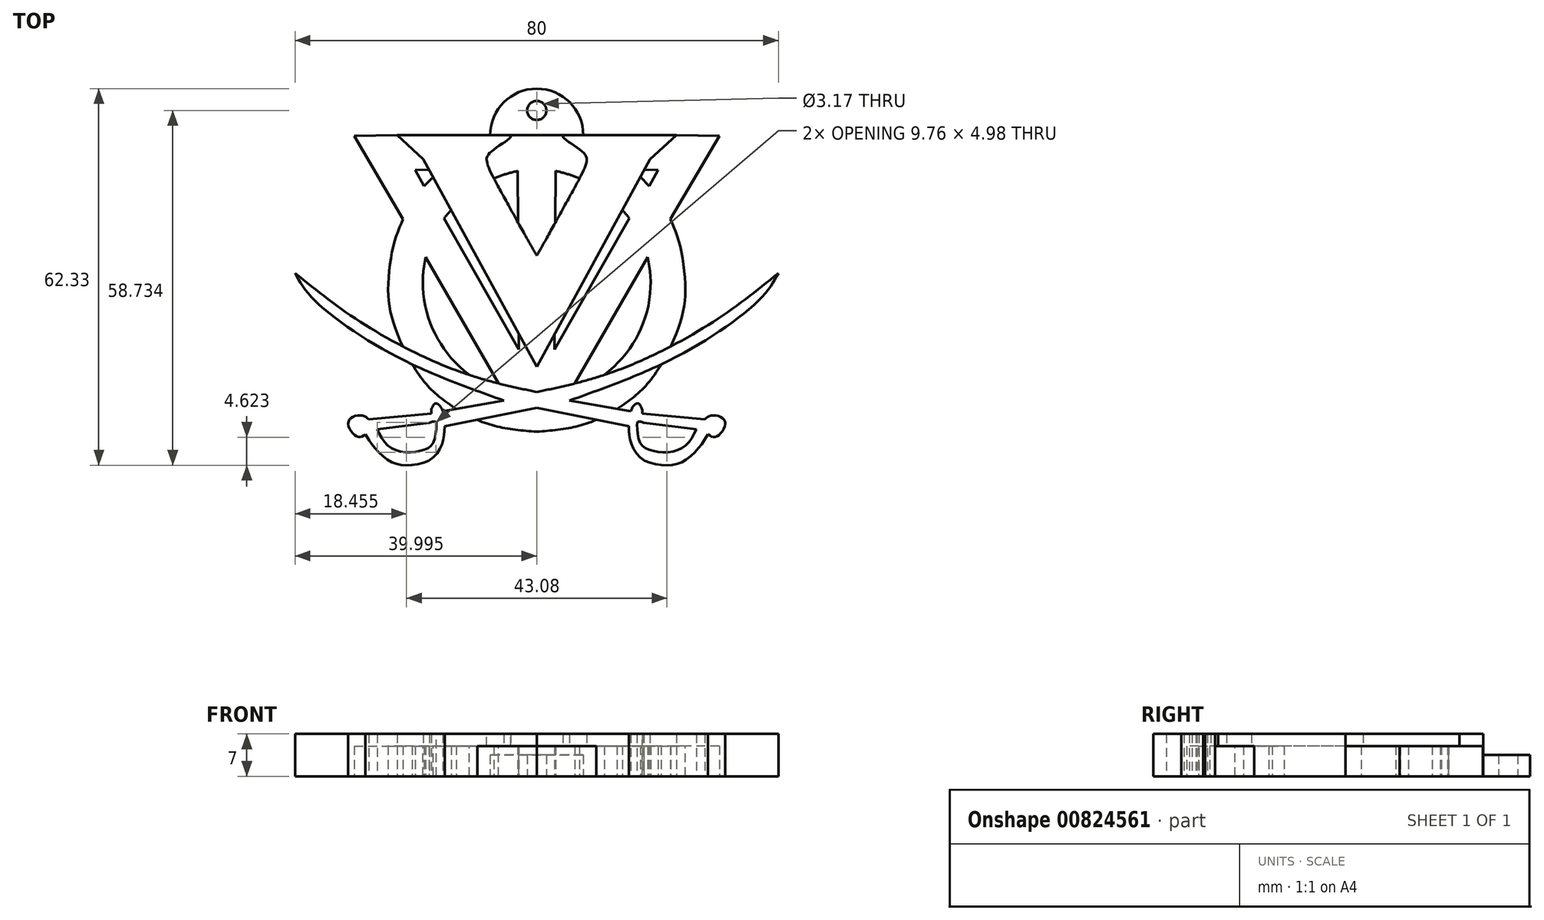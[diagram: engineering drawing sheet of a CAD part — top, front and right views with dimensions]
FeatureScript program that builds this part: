
annotation { "Feature Type Name" : "Feature", "Feature Type Description" : "" }
export const myFeature = defineFeature(function(context is Context, id is Id, definition is map)
    precondition{}
    {
        {
            var Q0;
            Q0=qCreatedBy(makeId("Top.planeOp"),FACE);
            var sketch = newSketch(context, id + "F0", { "sketchPlane" : qUnion([Q0])});
            skLineSegment(sketch, "E0", {"start": v(-25.22, 10.5) * mm, "end": v(-6.43, 10.5) * mm});
            skLineSegment(sketch, "E1", {"start": v(-25.22, 10.5) * mm, "end": v(-20.86, 6.51) * mm});
            skLineSegment(sketch, "E2", {"start": v(-20.86, 6.51) * mm, "end": v(-2.11, -27.86) * mm});
            skFitSpline(sketch, "E3", {"points": [v(-2.11, -32.02) * mm, v(-15.16, -28.54) * mm, v(-31.06, -20.55) * mm, v(-42.11, -12.34) * mm], "startDerivative": vector(-39.94, 8.48) * mm, "endDerivative": vector(-32.07, 25.88) * mm});
            skFitSpline(sketch, "E4", {"points": [v(-42.11, -12.34) * mm, v(-39.28, -16.4) * mm, v(-26.1, -25.73) * mm, v(-7.53, -33.43) * mm], "startDerivative": vector(9.94, -18.28) * mm, "endDerivative": vector(45.1, -16.07) * mm});
            skFitSpline(sketch, "E5", {"points": [v(-7.53, -33.43) * mm, v(-17.67, -35.2) * mm], "startDerivative": vector(-10.14, -1.78) * mm, "endDerivative": vector(-10.14, -1.78) * mm});
            skFitSpline(sketch, "E6", {"points": [v(-17.67, -35.2) * mm, v(-18.15, -34.28) * mm, v(-18.87, -33.9) * mm, v(-19.52, -34.81) * mm, v(-19.58, -35.55) * mm], "startDerivative": vector(-1.44, 3.67) * mm, "endDerivative": vector(0.2, -2.99) * mm});
            skFitSpline(sketch, "E7", {"points": [v(-19.58, -35.55) * mm, v(-29.94, -36.56) * mm], "startDerivative": vector(-10.36, -1.01) * mm, "endDerivative": vector(-10.36, -1.01) * mm});
            skFitSpline(sketch, "E8", {"points": [v(-29.94, -36.56) * mm, v(-30.68, -36) * mm, v(-32.31, -36.04) * mm, v(-33.32, -37.05) * mm, v(-32.66, -38.72) * mm, v(-31.48, -39.47) * mm, v(-30.46, -39.03) * mm], "startDerivative": vector(-4.52, 4.85) * mm, "endDerivative": vector(6.61, 4.5) * mm});
            skFitSpline(sketch, "E9", {"points": [v(-30.46, -39.03) * mm, v(-29.4, -40.66) * mm, v(-26.68, -43.34) * mm, v(-23.6, -44.13) * mm, v(-19.58, -43.12) * mm, v(-17.67, -40.26) * mm, v(-17.35, -37.7) * mm], "startDerivative": vector(6.67, -11.42) * mm, "endDerivative": vector(0.59, 16.46) * mm});
            skLineSegment(sketch, "E10", {"start": v(-17.35, -37.7) * mm, "end": v(-2.11, -34.63) * mm});
            skFitSpline(sketch, "E11", {"points": [v(-6.43, 10.5) * mm, v(-6.52, 10.1) * mm, v(-8.55, 8.64) * mm, v(-10.26, 7.08) * mm, v(-10.38, 6.19) * mm, v(-9.8, 4.56) * mm, v(-7.67, 0.53) * mm, v(-3.54, -6.95) * mm, v(-2.11, -9.4) * mm], "startDerivative": vector(0.4, -7.36) * mm, "endDerivative": vector(9.07, -15.38) * mm});
            skFitSpline(sketch, "E12.MirrorCS", {"points": [v(2.2, 10.5) * mm, v(2.29, 10.1) * mm, v(4.32, 8.64) * mm, v(6.03, 7.08) * mm, v(6.15, 6.19) * mm, v(5.58, 4.56) * mm, v(3.44, 0.53) * mm, v(-0.7, -6.95) * mm, v(-2.11, -9.4) * mm], "startDerivative": vector(-0.4, -7.36) * mm, "endDerivative": vector(-9.07, -15.38) * mm});
            skLineSegment(sketch, "E13.MirrorCS", {"start": v(20.99, 10.5) * mm, "end": v(2.2, 10.5) * mm});
            skLineSegment(sketch, "E14.MirrorCS", {"start": v(16.63, 6.51) * mm, "end": v(-2.11, -27.86) * mm});
            skLineSegment(sketch, "E15.MirrorCS", {"start": v(20.99, 10.5) * mm, "end": v(16.63, 6.51) * mm});
            skFitSpline(sketch, "E16.MirrorCS", {"points": [v(-2.11, -32.02) * mm, v(10.93, -28.54) * mm, v(26.83, -20.55) * mm, v(37.89, -12.34) * mm], "startDerivative": vector(39.94, 8.48) * mm, "endDerivative": vector(32.07, 25.88) * mm});
            skFitSpline(sketch, "E17.MirrorCS", {"points": [v(37.89, -12.34) * mm, v(35.05, -16.4) * mm, v(21.88, -25.73) * mm, v(3.3, -33.43) * mm], "startDerivative": vector(-9.94, -18.28) * mm, "endDerivative": vector(-45.1, -16.07) * mm});
            skFitSpline(sketch, "E18.MirrorCS", {"points": [v(3.3, -33.43) * mm, v(13.44, -35.2) * mm], "startDerivative": vector(10.14, -1.78) * mm, "endDerivative": vector(10.14, -1.78) * mm});
            skFitSpline(sketch, "E19.MirrorCS", {"points": [v(13.44, -35.2) * mm, v(13.92, -34.28) * mm, v(14.64, -33.9) * mm, v(15.3, -34.81) * mm, v(15.35, -35.55) * mm], "startDerivative": vector(1.44, 3.67) * mm, "endDerivative": vector(-0.2, -2.99) * mm});
            skFitSpline(sketch, "E20.MirrorCS", {"points": [v(15.35, -35.55) * mm, v(25.7, -36.56) * mm], "startDerivative": vector(10.36, -1.01) * mm, "endDerivative": vector(10.36, -1.01) * mm});
            skFitSpline(sketch, "E21.MirrorCS", {"points": [v(25.7, -36.56) * mm, v(26.46, -36) * mm, v(28.08, -36.04) * mm, v(29.1, -37.05) * mm, v(28.43, -38.72) * mm, v(27.25, -39.47) * mm, v(26.24, -39.03) * mm], "startDerivative": vector(4.52, 4.85) * mm, "endDerivative": vector(-6.61, 4.5) * mm});
            skFitSpline(sketch, "E22.MirrorCS", {"points": [v(26.24, -39.03) * mm, v(25.18, -40.66) * mm, v(22.45, -43.34) * mm, v(19.37, -44.13) * mm, v(15.35, -43.12) * mm, v(13.44, -40.26) * mm, v(13.12, -37.7) * mm], "startDerivative": vector(-6.67, -11.42) * mm, "endDerivative": vector(-0.59, 16.46) * mm});
            skLineSegment(sketch, "E23.MirrorCS", {"start": v(13.12, -37.7) * mm, "end": v(-2.11, -34.63) * mm});
            skLineSegment(sketch, "E24", {"start": v(-32.33, 10.4) * mm, "end": v(-25.22, 10.5) * mm});
            skLineSegment(sketch, "E25", {"start": v(-6.43, 10.5) * mm, "end": v(-2.11, 10.5) * mm});
            skLineSegment(sketch, "E26", {"start": v(-32.33, 10.4) * mm, "end": v(-24.25, -3.37) * mm});
            skPoint(sketch, "E27.7.internal.snap0", {"position": v(-2.14, -38.58) * mm});
            skFitSpline(sketch, "E27", {"points": [v(-24.25, -3.37) * mm, v(-25.82, -7.77) * mm, v(-26.7, -15.3) * mm, v(-25.56, -21.37) * mm, v(-21.37, -29.48) * mm, v(-16.5, -34.08) * mm, v(-9.76, -37.43) * mm, v(-2.11, -38.58) * mm], "startDerivative": vector(-14.53, -34.1) * mm, "endDerivative": vector(51.7, -4.04) * mm});
            skLineSegment(sketch, "E28", {"start": v(-22.21, 4.74) * mm, "end": v(-20.74, 2.05) * mm});
            skLineSegment(sketch, "E29", {"start": v(-20.74, 2.05) * mm, "end": v(-18.02, 4.84) * mm});
            skLineSegment(sketch, "E30", {"start": v(-18.02, 4.84) * mm, "end": v(-22.21, 4.74) * mm});
            skLineSegment(sketch, "E31", {"start": v(-20.48, -9.7) * mm, "end": v(-7.56, -32.1) * mm});
            skFitSpline(sketch, "E32", {"points": [v(-20.48, -9.7) * mm, v(-20.95, -13.05) * mm, v(-20.48, -18.18) * mm, v(-18.65, -22.94) * mm, v(-15.83, -26.86) * mm, v(-11.48, -30.42) * mm, v(-7.56, -32.1) * mm], "startDerivative": vector(-4.35, -22.23) * mm, "endDerivative": vector(24.5, -8.47) * mm});
            skFitSpline(sketch, "E33", {"points": [v(-5.24, 4.58) * mm, v(-12.79, 1.4) * mm, v(-17.45, -3.26) * mm], "startDerivative": vector(-17.16, -3.73) * mm, "endDerivative": vector(-8.8, -10.76) * mm});
            skLineSegment(sketch, "E34", {"start": v(-17.45, -3.26) * mm, "end": v(-5.05, -25) * mm});
            skLineSegment(sketch, "E35", {"start": v(-5.05, -25) * mm, "end": v(-5.24, 4.58) * mm});
            skLineSegment(sketch, "E36.MirrorCS", {"start": v(0.82, -25) * mm, "end": v(1.01, 4.58) * mm});
            skFitSpline(sketch, "E37.MirrorCS", {"points": [v(1.01, 4.58) * mm, v(8.56, 1.4) * mm, v(13.22, -3.26) * mm], "startDerivative": vector(17.16, -3.73) * mm, "endDerivative": vector(8.8, -10.76) * mm});
            skLineSegment(sketch, "E38.MirrorCS", {"start": v(17.98, 4.74) * mm, "end": v(16.51, 2.05) * mm});
            skLineSegment(sketch, "E39.MirrorCS", {"start": v(16.51, 2.05) * mm, "end": v(13.8, 4.84) * mm});
            skLineSegment(sketch, "E40.MirrorCS", {"start": v(13.8, 4.84) * mm, "end": v(17.98, 4.74) * mm});
            skFitSpline(sketch, "E41.MirrorCS", {"points": [v(20.02, -3.37) * mm, v(21.6, -7.77) * mm, v(22.48, -15.3) * mm, v(21.33, -21.37) * mm, v(17.14, -29.48) * mm, v(12.28, -34.08) * mm, v(5.53, -37.43) * mm, v(-2.11, -38.58) * mm], "startDerivative": vector(14.53, -34.1) * mm, "endDerivative": vector(-51.7, -4.04) * mm});
            skFitSpline(sketch, "E42.MirrorCS", {"points": [v(16.25, -9.7) * mm, v(16.72, -13.05) * mm, v(16.25, -18.18) * mm, v(14.42, -22.94) * mm, v(11.6, -26.86) * mm, v(7.26, -30.42) * mm, v(3.33, -32.1) * mm], "startDerivative": vector(4.35, -22.23) * mm, "endDerivative": vector(-24.5, -8.47) * mm});
            skLineSegment(sketch, "E43.MirrorCS", {"start": v(16.25, -9.7) * mm, "end": v(3.33, -32.1) * mm});
            skLineSegment(sketch, "E44.MirrorCS", {"start": v(13.22, -3.26) * mm, "end": v(0.82, -25) * mm});
            skLineSegment(sketch, "E45.MirrorCS", {"start": v(28.1, 10.4) * mm, "end": v(20.02, -3.37) * mm});
            skLineSegment(sketch, "E46.MirrorCS", {"start": v(28.1, 10.4) * mm, "end": v(20.99, 10.5) * mm});
            skLineSegment(sketch, "E47.MirrorCS", {"start": v(2.2, 10.5) * mm, "end": v(-2.11, 10.5) * mm});
            skFitSpline(sketch, "E48", {"points": [v(-28.53, -38.17) * mm, v(-19.88, -37.1) * mm], "startDerivative": vector(8.66, 1.07) * mm, "endDerivative": vector(8.66, 1.07) * mm});
            skFitSpline(sketch, "E49", {"points": [v(-28.53, -38.17) * mm, v(-26.76, -40.87) * mm, v(-23.8, -41.98) * mm, v(-20.62, -41.53) * mm, v(-19.18, -40.27) * mm, v(-18.73, -37.46) * mm, v(-18.88, -36.9) * mm, v(-19.88, -37.1) * mm], "startDerivative": vector(8.42, -17.19) * mm, "endDerivative": vector(-12.37, -4.06) * mm});
            skFitSpline(sketch, "E50.MirrorCS", {"points": [v(24.3, -38.17) * mm, v(15.65, -37.1) * mm], "startDerivative": vector(-8.66, 1.07) * mm, "endDerivative": vector(-8.66, 1.07) * mm});
            skFitSpline(sketch, "E51.MirrorCS", {"points": [v(24.3, -38.17) * mm, v(22.53, -40.87) * mm, v(19.57, -41.98) * mm, v(16.39, -41.53) * mm, v(14.95, -40.27) * mm, v(14.5, -37.46) * mm, v(14.65, -36.9) * mm, v(15.65, -37.1) * mm], "startDerivative": vector(-8.42, -17.19) * mm, "endDerivative": vector(12.37, -4.06) * mm});
            skCircle(sketch, "E52", {"center": v(-2.11, 14.6) * mm, "radius": 1.59 * mm});
            skArc(sketch, "E53", {"start": v(5.6, 10.5) * mm, "mid": v(-2.11, 18.2) * mm, "end": v(-9.82, 10.5) * mm});
            skSolve(sketch);
        }
        {
            var Q0;
            {var subQ9=sQuery(id+"F0.wireOp",EDGE,"E0");Q0=makeQuery(id+"F0.imprint","IMPRINT",FACE,{"disambiguationData":[TD([[makeQuery(id+"F0.imprint","IMPRINT",EDGE,{"derivedFrom":subQ9}),-1.0]])]});}
            var Q1;
            {var subQ0=sQuery(id+"F0.wireOp",EDGE,"E33");var subQ1=sQuery(id+"F0.wireOp",EDGE,"E2");var subQ2=makeQuery(id+"F0.imprint","INTERSECT",VERTEX,{"derivedFrom":[subQ1,subQ0]});Q1=makeQuery(id+"F0.imprint","IMPRINT",FACE,{"disambiguationData":[TD([[makeQuery(id+"F0.imprint","IMPRINT",EDGE,{"disambiguationData":[TD([[subQ2,-1.0]])],"derivedFrom":subQ1}),1.0]])]});}
            var Q2;
            {var subQ0=sQuery(id+"F0.wireOp",EDGE,"E14.MirrorCS");var subQ1=sQuery(id+"F0.wireOp",EDGE,"E2");var subQ2=makeQuery(id+"F0.imprint","INTERSECT",VERTEX,{"derivedFrom":[subQ1,subQ0]});Q2=makeQuery(id+"F0.imprint","IMPRINT",FACE,{"disambiguationData":[TD([[makeQuery(id+"F0.imprint","IMPRINT",EDGE,{"disambiguationData":[TD([[subQ2,1.0]])],"derivedFrom":subQ1}),1.0]])]});}
            var Q3;
            {var subQ0=sQuery(id+"F0.wireOp",EDGE,"E37.MirrorCS");var subQ1=sQuery(id+"F0.wireOp",EDGE,"E12.MirrorCS");var subQ2=makeQuery(id+"F0.imprint","INTERSECT",VERTEX,{"derivedFrom":[subQ1,subQ0]});Q3=makeQuery(id+"F0.imprint","IMPRINT",FACE,{"disambiguationData":[TD([[makeQuery(id+"F0.imprint","IMPRINT",EDGE,{"disambiguationData":[TD([[subQ2,-1.0]])],"derivedFrom":subQ1}),1.0]])]});}
            var Q4;
            {var subQ8=sQuery(id+"F0.wireOp",EDGE,"E13.MirrorCS");Q4=makeQuery(id+"F0.imprint","IMPRINT",FACE,{"disambiguationData":[TD([[makeQuery(id+"F0.imprint","IMPRINT",EDGE,{"derivedFrom":subQ8}),1.0]])]});}
            var Q5;
            {var subQ0=sQuery(id+"F0.wireOp",EDGE,"E17.MirrorCS");var subQ1=sQuery(id+"F0.wireOp",EDGE,"E16.MirrorCS");var subQ2=makeQuery(id+"F0.imprint","INTERSECT",VERTEX,{"derivedFrom":[subQ1,subQ0]});Q5=makeQuery(id+"F0.imprint","IMPRINT",FACE,{"disambiguationData":[TD([[makeQuery(id+"F0.imprint","IMPRINT",EDGE,{"disambiguationData":[TD([[subQ2,1.0]])],"derivedFrom":subQ1}),-1.0]])]});}
            var Q6;
            {var subQ8=sQuery(id+"F0.wireOp",EDGE,"E3");var subQ14=sQuery(id+"F0.wireOp",EDGE,"E16.MirrorCS");var subQ24=makeQuery(id+"F0.imprint","INTERSECT",VERTEX,{"derivedFrom":[subQ8,subQ14]});Q6=makeQuery(id+"F0.imprint","IMPRINT",FACE,{"disambiguationData":[TD([[makeQuery(id+"F0.imprint","IMPRINT",EDGE,{"disambiguationData":[TD([[subQ24,-1.0]])],"derivedFrom":subQ8}),1.0]])]});}
            var Q7;
            {var subQ0=sQuery(id+"F0.wireOp",EDGE,"E31");var subQ1=sQuery(id+"F0.wireOp",EDGE,"E3");var subQ2=makeQuery(id+"F0.imprint","INTERSECT",VERTEX,{"derivedFrom":[subQ1,subQ0]});Q7=makeQuery(id+"F0.imprint","IMPRINT",FACE,{"disambiguationData":[TD([[makeQuery(id+"F0.imprint","IMPRINT",EDGE,{"disambiguationData":[TD([[subQ2,-1.0]])],"derivedFrom":subQ1}),1.0]])]});}
            var Q8;
            {var subQ0=sQuery(id+"F0.wireOp",EDGE,"E43.MirrorCS");var subQ1=sQuery(id+"F0.wireOp",EDGE,"E16.MirrorCS");var subQ2=makeQuery(id+"F0.imprint","INTERSECT",VERTEX,{"derivedFrom":[subQ1,subQ0]});Q8=makeQuery(id+"F0.imprint","IMPRINT",FACE,{"disambiguationData":[TD([[makeQuery(id+"F0.imprint","IMPRINT",EDGE,{"disambiguationData":[TD([[subQ2,-1.0]])],"derivedFrom":subQ1}),-1.0]])]});}
            var Q9;
            {var subQ0=sQuery(id+"F0.wireOp",EDGE,"E6");Q9=makeQuery(id+"F0.imprint","IMPRINT",FACE,{"disambiguationData":[TD([[makeQuery(id+"F0.imprint","IMPRINT",EDGE,{"derivedFrom":subQ0}),1.0]])]});}
            var Q10;
            {var subQ0=sQuery(id+"F0.wireOp",EDGE,"E19.MirrorCS");Q10=makeQuery(id+"F0.imprint","IMPRINT",FACE,{"disambiguationData":[TD([[makeQuery(id+"F0.imprint","IMPRINT",EDGE,{"derivedFrom":subQ0}),-1.0]])]});}
            var Q11;
            {var subQ0=sQuery(id+"F0.wireOp",EDGE,"E4");var subQ1=sQuery(id+"F0.wireOp",EDGE,"E3");var subQ2=makeQuery(id+"F0.imprint","INTERSECT",VERTEX,{"derivedFrom":[subQ1,subQ0]});Q11=makeQuery(id+"F0.imprint","IMPRINT",FACE,{"disambiguationData":[TD([[makeQuery(id+"F0.imprint","IMPRINT",EDGE,{"disambiguationData":[TD([[subQ2,1.0]])],"derivedFrom":subQ1}),1.0]])]});}
            var Q12;
            {var subQ0=sQuery(id+"F0.wireOp",EDGE,"E30");var subQ1=sQuery(id+"F0.wireOp",EDGE,"E2");var subQ2=makeQuery(id+"F0.imprint","INTERSECT",VERTEX,{"derivedFrom":[subQ1,subQ0]});Q12=makeQuery(id+"F0.imprint","IMPRINT",FACE,{"disambiguationData":[TD([[makeQuery(id+"F0.imprint","IMPRINT",EDGE,{"disambiguationData":[TD([[subQ2,-1.0]])],"derivedFrom":subQ1}),1.0]])]});}
            var Q13;
            {var subQ0=sQuery(id+"F0.wireOp",EDGE,"E40.MirrorCS");var subQ1=sQuery(id+"F0.wireOp",EDGE,"E14.MirrorCS");var subQ2=makeQuery(id+"F0.imprint","INTERSECT",VERTEX,{"derivedFrom":[subQ1,subQ0]});Q13=makeQuery(id+"F0.imprint","IMPRINT",FACE,{"disambiguationData":[TD([[makeQuery(id+"F0.imprint","IMPRINT",EDGE,{"disambiguationData":[TD([[subQ2,-1.0]])],"derivedFrom":subQ1}),-1.0]])]});}
            extrude(context, id + "F1", {"entities" : qUnion([Q0, Q1, Q2, Q3, Q4, Q5, Q6, Q7, Q8, Q9, Q10, Q11, Q12, Q13]), "depth" : 7 * mm, "offsetDistance" : 25 * mm});
        }
        {
            var Q0;
            {var subQ8=sQuery(id+"F0.wireOp",EDGE,"E13.MirrorCS");Q0=makeQuery(id+"F0.imprint","IMPRINT",FACE,{"disambiguationData":[TD([[makeQuery(id+"F0.imprint","IMPRINT",EDGE,{"derivedFrom":subQ8}),1.0]])]});}
            var Q1;
            {var subQ27=sQuery(id+"F0.wireOp",EDGE,"E1");Q1=makeQuery(id+"F0.imprint","IMPRINT",FACE,{"disambiguationData":[TD([[makeQuery(id+"F0.imprint","IMPRINT",EDGE,{"derivedFrom":subQ27}),-1.0]])]});}
            var Q2;
            {var subQ10=sQuery(id+"F0.wireOp",EDGE,"E25");Q2=makeQuery(id+"F0.imprint","IMPRINT",FACE,{"disambiguationData":[TD([[makeQuery(id+"F0.imprint","IMPRINT",EDGE,{"derivedFrom":subQ10}),-1.0]])]});}
            var Q3;
            {var subQ0=sQuery(id+"F0.wireOp",EDGE,"E14.MirrorCS");var subQ1=sQuery(id+"F0.wireOp",EDGE,"E2");var subQ2=makeQuery(id+"F0.imprint","INTERSECT",VERTEX,{"derivedFrom":[subQ1,subQ0]});Q3=makeQuery(id+"F0.imprint","IMPRINT",FACE,{"disambiguationData":[TD([[makeQuery(id+"F0.imprint","IMPRINT",EDGE,{"disambiguationData":[TD([[subQ2,1.0]])],"derivedFrom":subQ1}),1.0]])]});}
            var Q4;
            {var subQ0=sQuery(id+"F0.wireOp",EDGE,"E23.MirrorCS");var subQ1=sQuery(id+"F0.wireOp",EDGE,"E10");var subQ2=makeQuery(id+"F0.imprint","INTERSECT",VERTEX,{"derivedFrom":[subQ1,subQ0]});Q4=makeQuery(id+"F0.imprint","IMPRINT",FACE,{"disambiguationData":[TD([[makeQuery(id+"F0.imprint","IMPRINT",EDGE,{"disambiguationData":[TD([[subQ2,1.0]])],"derivedFrom":subQ1}),-1.0]])]});}
            var Q5;
            {var subQ0=sQuery(id+"F0.wireOp",EDGE,"E18.MirrorCS");var subQ1=sQuery(id+"F0.wireOp",EDGE,"E17.MirrorCS");var subQ2=makeQuery(id+"F0.imprint","INTERSECT",VERTEX,{"derivedFrom":[subQ1,subQ0]});Q5=makeQuery(id+"F0.imprint","IMPRINT",FACE,{"disambiguationData":[TD([[makeQuery(id+"F0.imprint","IMPRINT",EDGE,{"disambiguationData":[TD([[subQ2,1.0]])],"derivedFrom":subQ1}),1.0]])]});}
            var Q6;
            {var subQ0=sQuery(id+"F0.wireOp",EDGE,"E5");var subQ1=sQuery(id+"F0.wireOp",EDGE,"E4");var subQ2=makeQuery(id+"F0.imprint","INTERSECT",VERTEX,{"derivedFrom":[subQ1,subQ0]});Q6=makeQuery(id+"F0.imprint","IMPRINT",FACE,{"disambiguationData":[TD([[makeQuery(id+"F0.imprint","IMPRINT",EDGE,{"disambiguationData":[TD([[subQ2,1.0]])],"derivedFrom":subQ1}),-1.0]])]});}
            var Q7;
            {var subQ8=sQuery(id+"F0.wireOp",EDGE,"E3");var subQ14=sQuery(id+"F0.wireOp",EDGE,"E16.MirrorCS");var subQ24=makeQuery(id+"F0.imprint","INTERSECT",VERTEX,{"derivedFrom":[subQ8,subQ14]});Q7=makeQuery(id+"F0.imprint","IMPRINT",FACE,{"disambiguationData":[TD([[makeQuery(id+"F0.imprint","IMPRINT",EDGE,{"disambiguationData":[TD([[subQ24,-1.0]])],"derivedFrom":subQ8}),1.0]])]});}
            var Q8;
            {var subQ9=sQuery(id+"F0.wireOp",EDGE,"E0");Q8=makeQuery(id+"F0.imprint","IMPRINT",FACE,{"disambiguationData":[TD([[makeQuery(id+"F0.imprint","IMPRINT",EDGE,{"derivedFrom":subQ9}),-1.0]])]});}
            extrude(context, id + "F2", {"entities" : qUnion([Q0, Q1, Q2, Q3, Q4, Q5, Q6, Q7, Q8]), "operationType" : NewBodyOperationType.ADD, "depth" : 5 * mm, "offsetDistance" : 25 * mm});
        }
        {
            var Q0;
            {var subQ3=sQuery(id+"F0.wireOp",EDGE,"E25");Q0=makeQuery(id+"F0.imprint","IMPRINT",FACE,{"disambiguationData":[TD([[makeQuery(id+"F0.imprint","IMPRINT",EDGE,{"derivedFrom":subQ3}),1.0]])]});}
            var sketch = newSketch(context, id + "F3", { "sketchPlane" : qUnion([Q0])});
            skSolve(sketch);
        }
        {
            var Q0;
            Q0 = qSketchRegion(id + "F3", true);
            var Q1;
            {var subQ3=sQuery(id+"F0.wireOp",EDGE,"E25");Q1=makeQuery(id+"F0.imprint","IMPRINT",FACE,{"disambiguationData":[TD([[makeQuery(id+"F0.imprint","IMPRINT",EDGE,{"derivedFrom":subQ3}),1.0]])]});}
            extrude(context, id + "F4", {"entities" : qUnion([Q0, Q1]), "operationType" : NewBodyOperationType.ADD, "depth" : 3.5 * mm, "offsetDistance" : 25 * mm});
        }
    });
